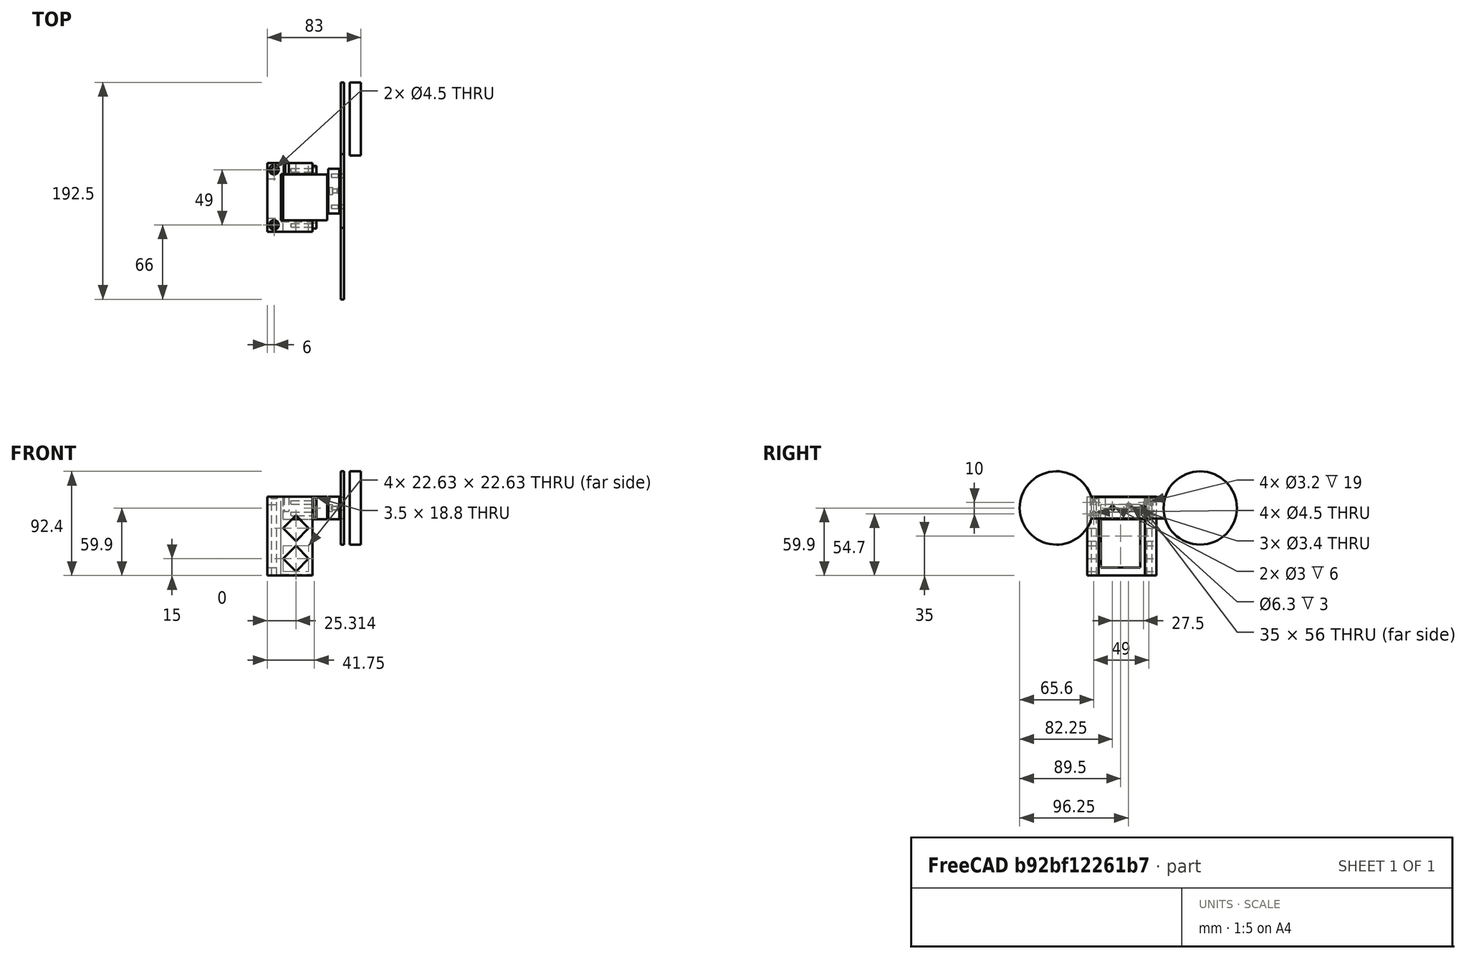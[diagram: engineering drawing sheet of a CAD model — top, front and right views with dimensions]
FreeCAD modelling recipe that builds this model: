
FCSTD DOCUMENT  (FreeCAD 0.19R24276 (Git))
Label: projector servo switch 0.1
License: All rights reserved
LicenseURL: http://en.wikipedia.org/wiki/All_rights_reserved
objects: Part::Cylinder×20, Part::Box×13, Part::Cut×12, Part::MultiFuse×11, Part::Chamfer×5, Part::Fuse×1, Part::Feature×1
note: 63 computed .brp shape members not serialized (recipe doc carries the construction recipe); baked Part::Feature solids carry a one-line shape summary decoded from their .brp

FEATURE [Part::Box] Box  label="Cube"
  AttacherType = Attacher::AttachEngine3D
  Height = 70
  Length = 40
  Width = 61
FEATURE [Part::Box] Box001  label="Cube001"
  AttacherType = Attacher::AttachEngine3D
  Height = 75
  Length = 28
  Placement = pos=(12,10,0) rot=(0,0,1;0rad)
  Width = 41
FEATURE [Part::Cut] Cut
  Base = -> Box
  Tool = -> Box001
FEATURE [Part::Box] Box002  label="Cube002"
  AttacherType = Attacher::AttachEngine3D
  Height = 19.8
  Length = 39
  Placement = pos=(14,10.25,50) rot=(0,0,1;0rad)
  Width = 40.5
FEATURE [Part::Box] Box003  label="Cube003"
  AttacherType = Attacher::AttachEngine3D
  Height = 18.8
  Length = 3.5
  Placement = pos=(40,2.75,50.5) rot=(0,0,1;0rad)
  Width = 7.5
FEATURE [Part::Box] Box004  label="Cube004"
  AttacherType = Attacher::AttachEngine3D
  Height = 18.8
  Length = 3.5
  Placement = pos=(40,50.75,50.5) rot=(0,0,1;0rad)
  Width = 7.5
FEATURE [Part::Cylinder] Cylinder
  Angle = 360
  AttacherType = Attacher::AttachEngine3D
  Height = 10
  Placement = pos=(36,5.6,64.7) rot=(0,1,0;1.5708rad)
  Radius = 2.25
FEATURE [Part::Cylinder] Cylinder001
  Angle = 360
  AttacherType = Attacher::AttachEngine3D
  Height = 10
  Placement = pos=(36,5.6,54.7) rot=(0,1,0;1.5708rad)
  Radius = 2.25
FEATURE [Part::Cylinder] Cylinder002
  Angle = 360
  AttacherType = Attacher::AttachEngine3D
  Height = 10
  Placement = pos=(36,54.6,64.7) rot=(0,1,0;1.5708rad)
  Radius = 2.25
FEATURE [Part::Cylinder] Cylinder003
  Angle = 360
  AttacherType = Attacher::AttachEngine3D
  Height = 10
  Placement = pos=(36,54.6,54.7) rot=(0,1,0;1.5708rad)
  Radius = 2.25
FEATURE [Part::Cylinder] Cylinder004
  Angle = 360
  AttacherType = Attacher::AttachEngine3D
  Height = 10
  Placement = pos=(45,36.25,59.9) rot=(0,1,0;1.5708rad)
  Radius = 2
FEATURE [Part::MultiFuse] Fusion
  Shapes = -> [Cylinder001,Cylinder]
FEATURE [Part::MultiFuse] Fusion001
  Shapes = -> [Cylinder002,Cylinder003]
FEATURE [Part::MultiFuse] Fusion002
  Shapes = -> [Box002,Box003,Box004]
FEATURE [Part::MultiFuse] Fusion003
  Shapes = -> [Fusion001,Fusion]
FEATURE [Part::Cut] Cut001
  Base = -> Fusion002
  Tool = -> Fusion003
FEATURE [Part::Cylinder] Cylinder005
  Angle = 360
  AttacherType = Attacher::AttachEngine3D
  Height = 21
  Placement = pos=(21,54.6,64.7) rot=(0,1,0;1.5708rad)
  Radius = 1.6
FEATURE [Part::Cylinder] Cylinder006
  Angle = 360
  AttacherType = Attacher::AttachEngine3D
  Height = 21
  Placement = pos=(21,54.6,54.7) rot=(0,1,0;1.5708rad)
  Radius = 1.6
FEATURE [Part::Cylinder] Cylinder007
  Angle = 360
  AttacherType = Attacher::AttachEngine3D
  Height = 21
  Placement = pos=(21,5.6,64.7) rot=(0,1,0;1.5708rad)
  Radius = 1.6
FEATURE [Part::Cylinder] Cylinder008
  Angle = 360
  AttacherType = Attacher::AttachEngine3D
  Height = 21
  Placement = pos=(21,5.6,54.7) rot=(0,1,0;1.5708rad)
  Radius = 1.6
FEATURE [Part::Box] Box005  label="Cube005"
  AttacherType = Attacher::AttachEngine3D
  Height = 14
  Length = 4
  Placement = pos=(15,49,57) rot=(0,0,1;0rad)
  Width = 16
FEATURE [Part::Fuse] Fusion004
  Base = -> Cylinder004
  Tool = -> Cut001
FEATURE [Part::MultiFuse] Fusion005
  Shapes = -> [Cylinder005,Cylinder006,Cylinder007,Cylinder008]
FEATURE [Part::Cut] Cut002
  Base = -> Cut
  Tool = -> Fusion005
FEATURE [Part::Cut] Cut003
  Base = -> Cut002
  Tool = -> Box005
FEATURE [Part::Cylinder] Cylinder009
  Angle = 360
  AttacherType = Attacher::AttachEngine3D
  Height = 74
  Placement = pos=(6,6,-2) rot=(0,0,1;0rad)
  Radius = 2.25
FEATURE [Part::Cylinder] Cylinder010
  Angle = 360
  AttacherType = Attacher::AttachEngine3D
  Height = 74
  Placement = pos=(6,55,-2) rot=(0,0,1;0rad)
  Radius = 2.25
FEATURE [Part::MultiFuse] Fusion006
  Shapes = -> [Cylinder009,Cylinder010]
FEATURE [Part::Cut] Cut004
  Base = -> Cut003
  Tool = -> Fusion006
FEATURE [Part::Chamfer] Chamfer
  Base = -> Cut004
  Edges = 2 edges r=2: [Edge14,Edge15]
FEATURE [Part::Box] Box006  label="Cube006"
  AttacherType = Attacher::AttachEngine3D
  Height = 20
  Length = 10
  Placement = pos=(54,16,50) rot=(0,0,1;0rad)
  Width = 40
FEATURE [Part::Cylinder] Cylinder011
  Angle = 360
  AttacherType = Attacher::AttachEngine3D
  Height = 10
  Placement = pos=(48,36.25,59.9) rot=(0,1,0;1.5708rad)
  Radius = 3.15
FEATURE [Part::Cut] Cut005
  Base = -> Box006
  Tool = -> Cylinder011
FEATURE [Part::Cylinder] Cylinder012
  Angle = 360
  AttacherType = Attacher::AttachEngine3D
  Height = 10
  Placement = pos=(57,36.25,59.9) rot=(0,1,0;1.5708rad)
  Radius = 1.7
FEATURE [Part::Cut] Cut006
  Base = -> Cut005
  Tool = -> Cylinder012
FEATURE [Part::Chamfer] Chamfer001
  Base = -> Cut006
  Edges = 1 edges r=2: [Edge16]
FEATURE [Part::Cylinder] Cylinder013
  Angle = 360
  AttacherType = Attacher::AttachEngine3D
  Height = 10
  Placement = pos=(57,49.75,59.9) rot=(0,1,0;1.5708rad)
  Radius = 1.5
FEATURE [Part::Cylinder] Cylinder014
  Angle = 360
  AttacherType = Attacher::AttachEngine3D
  Height = 10
  Placement = pos=(57,22.25,59.9) rot=(0,1,0;1.5708rad)
  Radius = 1.5
FEATURE [Part::MultiFuse] Fusion007
  Shapes = -> [Cylinder013,Cylinder014]
FEATURE [Part::Cut] Cut007
  Base = -> Chamfer001
  Tool = -> Fusion007
FEATURE [Part::Chamfer] Chamfer002
  Base = -> Cut007
  Edges = 2 edges r=1: [Edge5,Edge7]
FEATURE [Part::Box] Box007  label="Cube007"
  AttacherType = Attacher::AttachEngine3D
  Height = 19
  Length = 3
  Placement = pos=(65,-44,50.5) rot=(0,0,1;0rad)
  Width = 159
FEATURE [Part::Cylinder] Cylinder015
  Angle = 360
  AttacherType = Attacher::AttachEngine3D
  Height = 10
  Placement = pos=(73,100,59.9) rot=(0,1,0;1.5708rad)
  Radius = 32.5
FEATURE [Part::Cylinder] Cylinder016
  Angle = 360
  AttacherType = Attacher::AttachEngine3D
  Height = 3
  Placement = pos=(65,100,59.9) rot=(0,1,0;1.5708rad)
  Radius = 32.5
FEATURE [Part::Cylinder] Cylinder017
  Angle = 360
  AttacherType = Attacher::AttachEngine3D
  Height = 3
  Placement = pos=(65,-27.5,59.9) rot=(0,1,0;1.5708rad)
  Radius = 32.5
FEATURE [Part::Cylinder] Cylinder018
  Angle = 360
  AttacherType = Attacher::AttachEngine3D
  Height = 10
  Placement = pos=(62,22.25,59.9) rot=(0,1,0;1.5708rad)
  Radius = 1.7
FEATURE [Part::Cylinder] Cylinder019
  Angle = 360
  AttacherType = Attacher::AttachEngine3D
  Height = 10
  Placement = pos=(60,49.75,59.9) rot=(0,1,0;1.5708rad)
  Radius = 1.7
FEATURE [Part::MultiFuse] Fusion008
  Shapes = -> [Box007,Cylinder016,Cylinder017]
FEATURE [Part::MultiFuse] Fusion009
  Shapes = -> [Cylinder019,Cylinder018]
FEATURE [Part::Cut] Cut008
  Base = -> Fusion008
  Tool = -> Fusion009
FEATURE [Part::Feature] Cut008_cs
  Placement = pos=(0,0,0) rot=(0,1,0;1.5708rad)
  shape: bbox 65 x 192.5 x 3e-07 mm, 0 faces, 0 solids (baked)
FEATURE [Part::Chamfer] Chamfer003
  Base = -> Chamfer002
  Edges = 1 edges r=1: [Edge24]
FEATURE [Part::Chamfer] Chamfer004
  Base = -> Chamfer
  Edges = 4 edges r=1: [Edge22,Edge23,Edge38,Edge39]
FEATURE [Part::Box] Box008  label="Cube008"
  AttacherType = Attacher::AttachEngine3D
  Height = 56
  Length = 15
  Placement = pos=(-1,12,7) rot=(0,0,1;0rad)
  Width = 35
FEATURE [Part::Cut] Cut009
  Base = -> Chamfer004
  Tool = -> Box008
FEATURE [Part::Box] Box009  label="Cube009"
  AttacherType = Attacher::AttachEngine3D
  Height = 16
  Length = 16
  Placement = pos=(14,-1,15) rot=(0,1,0;0.785398rad)
  Width = 12
FEATURE [Part::Box] Box010  label="Cube010"
  AttacherType = Attacher::AttachEngine3D
  Height = 16
  Length = 16
  Placement = pos=(14,-1,42) rot=(0,1,0;0.785398rad)
  Width = 12
FEATURE [Part::MultiFuse] Fusion010
  Shapes = -> [Box009,Box010]
FEATURE [Part::Cut] Cut010
  Base = -> Cut009
  Tool = -> Fusion010
FEATURE [Part::Box] Box011  label="Cube011"
  AttacherType = Attacher::AttachEngine3D
  Height = 16
  Length = 16
  Placement = pos=(14,50,15) rot=(0,1,0;0.785398rad)
  Width = 12
FEATURE [Part::Box] Box012  label="Cube012"
  AttacherType = Attacher::AttachEngine3D
  Height = 16
  Length = 16
  Placement = pos=(14,50,42) rot=(0,1,0;0.785398rad)
  Width = 12
FEATURE [Part::MultiFuse] Fusion011
  Shapes = -> [Box011,Box012]
FEATURE [Part::Cut] Cut011
  Base = -> Cut010
  Tool = -> Fusion011
